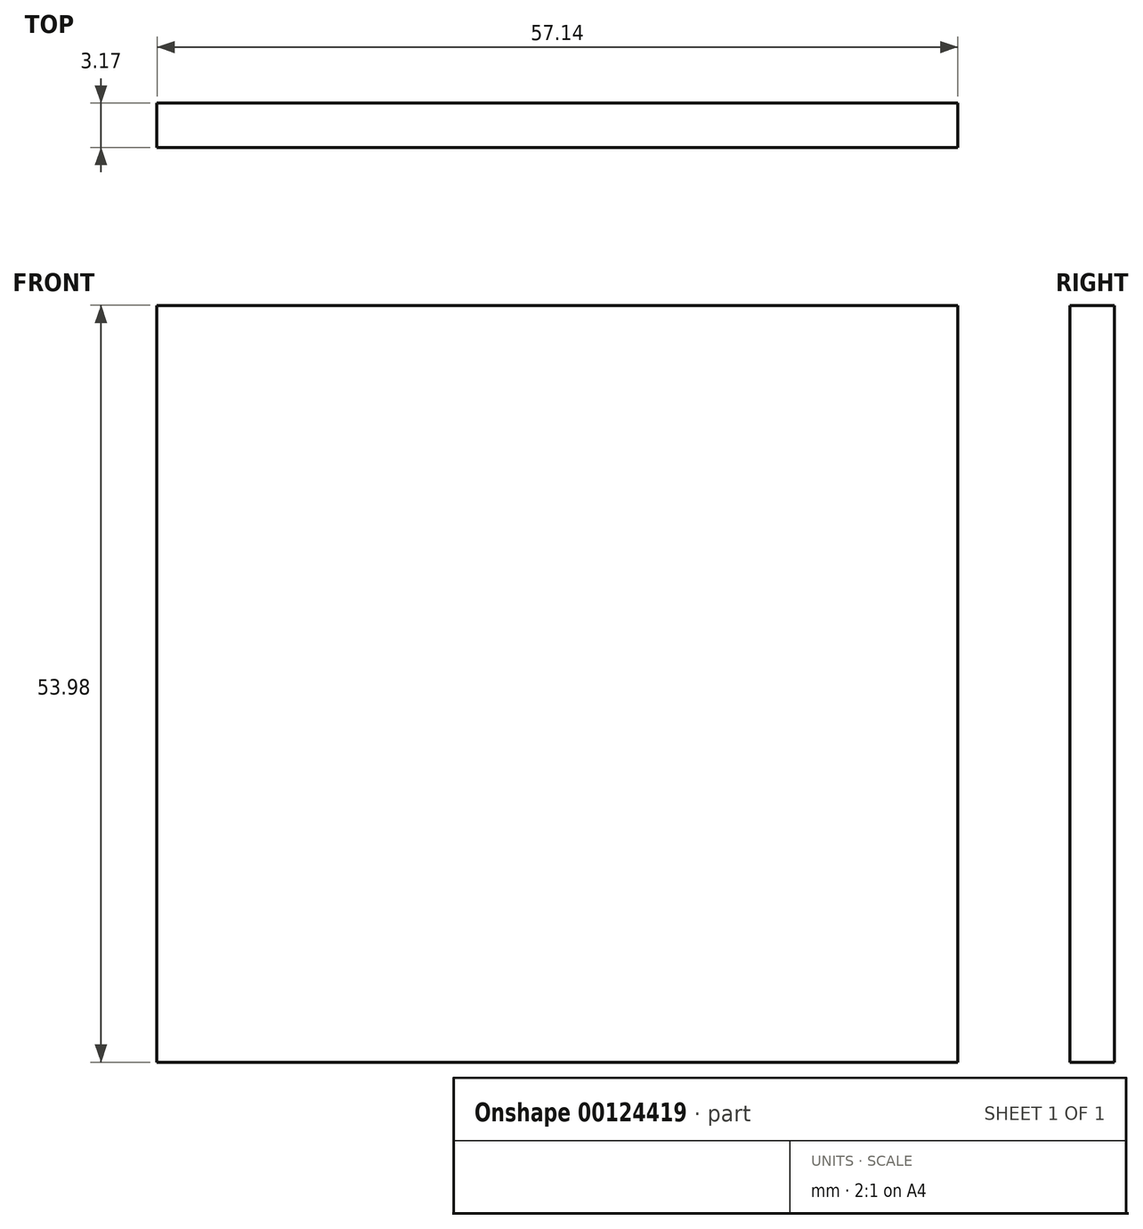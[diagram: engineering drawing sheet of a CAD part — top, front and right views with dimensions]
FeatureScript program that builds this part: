
annotation { "Feature Type Name" : "Feature", "Feature Type Description" : "" }
export const myFeature = defineFeature(function(context is Context, id is Id, definition is map)
    precondition{}
    {
        {
            var Q0;
            Q0=qCreatedBy(makeId("Front.planeOp"),FACE);
            var sketch = newSketch(context, id + "F0", { "sketchPlane" : qUnion([Q0])});
            skLineSegment(sketch, "E0.bottom", {"start": v(28.57, -26.99) * mm, "end": v(-28.58, -26.99) * mm});
            skLineSegment(sketch, "E0.top", {"start": v(28.57, 26.99) * mm, "end": v(-28.58, 26.99) * mm});
            skLineSegment(sketch, "E0.left", {"start": v(28.57, -26.99) * mm, "end": v(28.57, 26.99) * mm});
            skLineSegment(sketch, "E0.right", {"start": v(-28.58, -26.99) * mm, "end": v(-28.58, 26.99) * mm});
            skPoint(sketch, "E0.middle", {"position": v(0, 0) * mm});
            skSolve(sketch);
        }
        {
            var Q0;
            Q0 = qSketchRegion(id + "F0", true);
            extrude(context, id + "F1", {"entities" : qUnion([Q0]), "depth" : 3.17 * mm});
        }
    });
